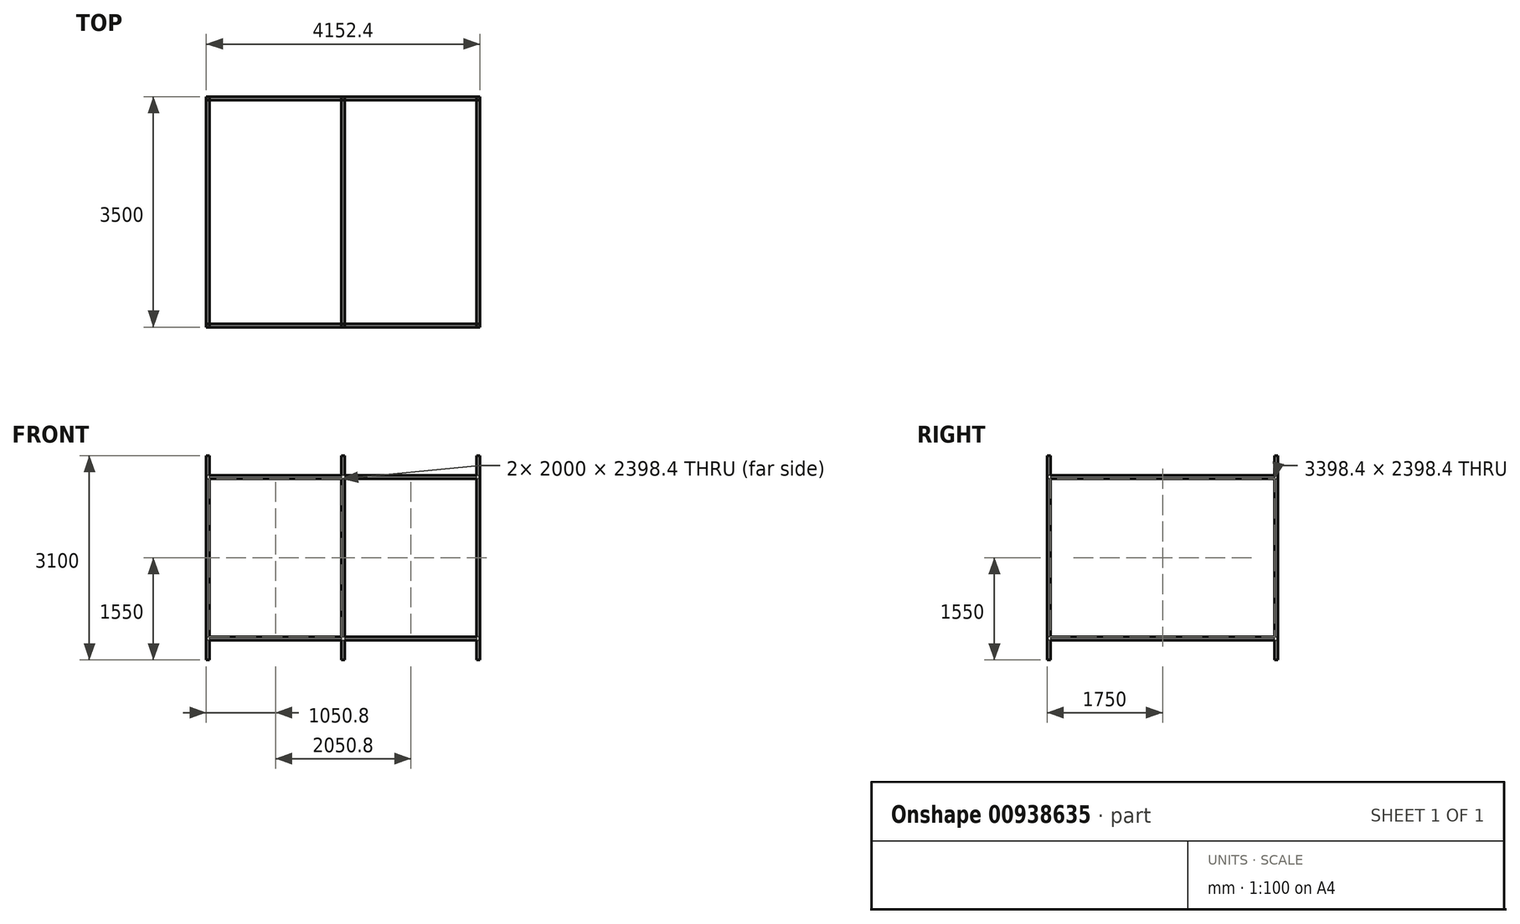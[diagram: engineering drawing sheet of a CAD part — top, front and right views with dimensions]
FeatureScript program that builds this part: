
annotation { "Feature Type Name" : "Feature", "Feature Type Description" : "" }
export const myFeature = defineFeature(function(context is Context, id is Id, definition is map)
    precondition{}
    {
        {
            var Q0;
            Q0=qCreatedBy(makeId("Right.planeOp"),FACE);
            var sketch = newSketch(context, id + "F0", { "sketchPlane" : qUnion([Q0])});
            skLineSegment(sketch, "E0.bottom", {"start": v(-1299.5, 1227.49) * mm, "end": v(2200.5, 1227.49) * mm});
            skLineSegment(sketch, "E0.top", {"start": v(-1299.5, -1272.51) * mm, "end": v(2200.5, -1272.51) * mm});
            skLineSegment(sketch, "E0.left", {"start": v(-1299.5, 1227.49) * mm, "end": v(-1299.5, -1272.51) * mm});
            skLineSegment(sketch, "E0.right", {"start": v(2200.5, 1227.49) * mm, "end": v(2200.5, -1272.51) * mm});
            skLineSegment(sketch, "E1.bottom", {"start": v(-1248.7, 1176.69) * mm, "end": v(2149.7, 1176.69) * mm});
            skLineSegment(sketch, "E1.top", {"start": v(-1248.7, -1221.71) * mm, "end": v(2149.7, -1221.71) * mm});
            skLineSegment(sketch, "E1.left", {"start": v(-1248.7, 1176.69) * mm, "end": v(-1248.7, -1221.71) * mm});
            skLineSegment(sketch, "E1.right", {"start": v(2149.7, 1176.69) * mm, "end": v(2149.7, -1221.71) * mm});
            skSolve(sketch);
        }
        {
            var Q0;
            Q0 = qSketchRegion(id + "F0", true);
            extrude(context, id + "F1", {"entities" : qUnion([Q0]), "depth" : 50.8 * mm, "offsetDistance" : 25.4 * mm});
        }
        {
            var Q0;
            Q0=makeQuery(id+"F1.opExtrude","SWEPT_FACE",FACE,{"disambiguationData":[OSD([sQuery(id+"F0.wireOp",EDGE,"E0.bottom")])]});
            var sketch = newSketch(context, id + "F2", { "sketchPlane" : qUnion([Q0])});
            skLineSegment(sketch, "E2.bottom", {"start": v(0, -1299.5) * mm, "end": v(50.8, -1299.5) * mm});
            skLineSegment(sketch, "E2.top", {"start": v(0, -1248.7) * mm, "end": v(50.8, -1248.7) * mm});
            skLineSegment(sketch, "E2.left", {"start": v(0, -1299.5) * mm, "end": v(0, -1248.7) * mm});
            skLineSegment(sketch, "E2.right", {"start": v(50.8, -1299.5) * mm, "end": v(50.8, -1248.7) * mm});
            skLineSegment(sketch, "E3.bottom", {"start": v(0, 2200.5) * mm, "end": v(50.8, 2200.5) * mm});
            skLineSegment(sketch, "E3.top", {"start": v(0, 2149.7) * mm, "end": v(50.8, 2149.7) * mm});
            skLineSegment(sketch, "E3.left", {"start": v(0, 2200.5) * mm, "end": v(0, 2149.7) * mm});
            skLineSegment(sketch, "E3.right", {"start": v(50.8, 2200.5) * mm, "end": v(50.8, 2149.7) * mm});
            skSolve(sketch);
        }
        {
            var Q0;
            Q0 = qSketchRegion(id + "F2", true);
            extrude(context, id + "F3", {"entities" : qUnion([Q0]), "operationType" : NewBodyOperationType.ADD, "depth" : 300 * mm, "offsetDistance" : 25.4 * mm});
        }
        {
            var Q0;
            Q0=makeQuery(id+"F1.opExtrude","SWEPT_FACE",FACE,{"disambiguationData":[OSD([sQuery(id+"F0.wireOp",EDGE,"E0.top")])]});
            var sketch = newSketch(context, id + "F4", { "sketchPlane" : qUnion([Q0])});
            skLineSegment(sketch, "E4.bottom", {"start": v(50.8, 1299.5) * mm, "end": v(0, 1299.5) * mm});
            skLineSegment(sketch, "E4.top", {"start": v(50.8, 1248.7) * mm, "end": v(0, 1248.7) * mm});
            skLineSegment(sketch, "E4.left", {"start": v(50.8, 1299.5) * mm, "end": v(50.8, 1248.7) * mm});
            skLineSegment(sketch, "E4.right", {"start": v(0, 1299.5) * mm, "end": v(0, 1248.7) * mm});
            skLineSegment(sketch, "E5.bottom", {"start": v(0, -2200.5) * mm, "end": v(50.8, -2200.5) * mm});
            skLineSegment(sketch, "E5.top", {"start": v(0, -2149.7) * mm, "end": v(50.8, -2149.7) * mm});
            skLineSegment(sketch, "E5.left", {"start": v(0, -2200.5) * mm, "end": v(0, -2149.7) * mm});
            skLineSegment(sketch, "E5.right", {"start": v(50.8, -2200.5) * mm, "end": v(50.8, -2149.7) * mm});
            skSolve(sketch);
        }
        {
            var Q0;
            Q0 = qSketchRegion(id + "F4", true);
            extrude(context, id + "F5", {"entities" : qUnion([Q0]), "operationType" : NewBodyOperationType.ADD, "depth" : 300 * mm, "offsetDistance" : 25.4 * mm});
        }
        {
            var Q0;
            Q0=makeQuery(id+"F5.boolean.opBoolean","MERGE",FACE,{"derivedFrom":[makeQuery(id+"F3.boolean.opBoolean","MERGE",FACE,{"derivedFrom":[makeQuery(id+"F1.opExtrude","CAP_FACE",FACE,{"disambiguationData":[OSD([sQuery(id+"F0.wireOp",EDGE,"E0.bottom"),sQuery(id+"F0.wireOp",EDGE,"E0.top"),sQuery(id+"F0.wireOp",EDGE,"E0.left"),sQuery(id+"F0.wireOp",EDGE,"E0.right"),sQuery(id+"F0.wireOp",EDGE,"E1.bottom"),sQuery(id+"F0.wireOp",EDGE,"E1.top"),sQuery(id+"F0.wireOp",EDGE,"E1.left"),sQuery(id+"F0.wireOp",EDGE,"E1.right")])],"isStart":true}),makeQuery(id+"F3.opExtrude","SWEPT_FACE",FACE,{"disambiguationData":[OSD([sQuery(id+"F2.wireOp",EDGE,"E2.left")])]}),makeQuery(id+"F3.opExtrude","SWEPT_FACE",FACE,{"disambiguationData":[OSD([sQuery(id+"F2.wireOp",EDGE,"E3.left")])]})]}),makeQuery(id+"F5.opExtrude","SWEPT_FACE",FACE,{"disambiguationData":[OSD([sQuery(id+"F4.wireOp",EDGE,"E4.right")])]}),makeQuery(id+"F5.opExtrude","SWEPT_FACE",FACE,{"disambiguationData":[OSD([sQuery(id+"F4.wireOp",EDGE,"E5.left")])]})]});
            var sketch = newSketch(context, id + "F6", { "sketchPlane" : qUnion([Q0])});
            skLineSegment(sketch, "E6.bottom", {"start": v(-2149.7, 1227.49) * mm, "end": v(-2200.5, 1227.49) * mm});
            skLineSegment(sketch, "E6.top", {"start": v(-2149.7, 1176.69) * mm, "end": v(-2200.5, 1176.69) * mm});
            skLineSegment(sketch, "E6.left", {"start": v(-2149.7, 1227.49) * mm, "end": v(-2149.7, 1176.69) * mm});
            skLineSegment(sketch, "E6.right", {"start": v(-2200.5, 1227.49) * mm, "end": v(-2200.5, 1176.69) * mm});
            skLineSegment(sketch, "E7.bottom", {"start": v(1248.7, 1176.69) * mm, "end": v(1299.5, 1176.69) * mm});
            skLineSegment(sketch, "E7.top", {"start": v(1248.7, 1227.49) * mm, "end": v(1299.5, 1227.49) * mm});
            skLineSegment(sketch, "E7.left", {"start": v(1248.7, 1176.69) * mm, "end": v(1248.7, 1227.49) * mm});
            skLineSegment(sketch, "E7.right", {"start": v(1299.5, 1176.69) * mm, "end": v(1299.5, 1227.49) * mm});
            skLineSegment(sketch, "E8.bottom", {"start": v(-2149.7, -1221.71) * mm, "end": v(-2200.5, -1221.71) * mm});
            skLineSegment(sketch, "E8.top", {"start": v(-2149.7, -1272.51) * mm, "end": v(-2200.5, -1272.51) * mm});
            skLineSegment(sketch, "E8.left", {"start": v(-2149.7, -1221.71) * mm, "end": v(-2149.7, -1272.51) * mm});
            skLineSegment(sketch, "E8.right", {"start": v(-2200.5, -1221.71) * mm, "end": v(-2200.5, -1272.51) * mm});
            skLineSegment(sketch, "E9.bottom", {"start": v(1248.7, -1221.71) * mm, "end": v(1299.5, -1221.71) * mm});
            skLineSegment(sketch, "E9.top", {"start": v(1248.7, -1272.51) * mm, "end": v(1299.5, -1272.51) * mm});
            skLineSegment(sketch, "E9.left", {"start": v(1248.7, -1221.71) * mm, "end": v(1248.7, -1272.51) * mm});
            skLineSegment(sketch, "E9.right", {"start": v(1299.5, -1221.71) * mm, "end": v(1299.5, -1272.51) * mm});
            skSolve(sketch);
        }
        {
            var Q0;
            Q0 = qSketchRegion(id + "F6", true);
            extrude(context, id + "F7", {"entities" : qUnion([Q0]), "operationType" : NewBodyOperationType.ADD, "depth" : 1000 * mm, "offsetDistance" : 25.4 * mm});
        }
        {
            var Q0;
            Q0=makeQuery(id+"F1.opExtrude","SWEPT_BODY",BODY,{"disambiguationData":[OSD([sQuery(id+"F0.wireOp",EDGE,"E0.bottom"),sQuery(id+"F0.wireOp",EDGE,"E0.top"),sQuery(id+"F0.wireOp",EDGE,"E0.left"),sQuery(id+"F0.wireOp",EDGE,"E0.right"),sQuery(id+"F0.wireOp",EDGE,"E1.bottom"),sQuery(id+"F0.wireOp",EDGE,"E1.top"),sQuery(id+"F0.wireOp",EDGE,"E1.left"),sQuery(id+"F0.wireOp",EDGE,"E1.right")])]});
            var Q1;
            Q1=makeQuery(id+"F7.opExtrude","CAP_FACE",FACE,{"disambiguationData":[OSD([sQuery(id+"F6.wireOp",EDGE,"E6.bottom"),sQuery(id+"F6.wireOp",EDGE,"E6.top"),sQuery(id+"F6.wireOp",EDGE,"E6.left"),sQuery(id+"F6.wireOp",EDGE,"E6.right")])],"isStart":false});
            mirror(context, id + "F8", {"operationType" : NewBodyOperationType.ADD, "entities" : qUnion([Q0]), "mirrorPlane" : qUnion([Q1])});
        }
        {
            var Q0;
            Q0=makeQuery(id+"F8.opPattern","COPY",FACE,{"derivedFrom":makeQuery(id+"F5.boolean.opBoolean","MERGE",FACE,{"derivedFrom":[makeQuery(id+"F3.boolean.opBoolean","MERGE",FACE,{"derivedFrom":[makeQuery(id+"F1.opExtrude","CAP_FACE",FACE,{"disambiguationData":[OSD([sQuery(id+"F0.wireOp",EDGE,"E0.bottom"),sQuery(id+"F0.wireOp",EDGE,"E0.top"),sQuery(id+"F0.wireOp",EDGE,"E0.left"),sQuery(id+"F0.wireOp",EDGE,"E0.right"),sQuery(id+"F0.wireOp",EDGE,"E1.bottom"),sQuery(id+"F0.wireOp",EDGE,"E1.top"),sQuery(id+"F0.wireOp",EDGE,"E1.left"),sQuery(id+"F0.wireOp",EDGE,"E1.right")])],"isStart":false}),makeQuery(id+"F3.opExtrude","SWEPT_FACE",FACE,{"disambiguationData":[OSD([sQuery(id+"F2.wireOp",EDGE,"E2.right")])]}),makeQuery(id+"F3.opExtrude","SWEPT_FACE",FACE,{"disambiguationData":[OSD([sQuery(id+"F2.wireOp",EDGE,"E3.right")])]})]}),makeQuery(id+"F5.opExtrude","SWEPT_FACE",FACE,{"disambiguationData":[OSD([sQuery(id+"F4.wireOp",EDGE,"E4.left")])]}),makeQuery(id+"F5.opExtrude","SWEPT_FACE",FACE,{"disambiguationData":[OSD([sQuery(id+"F4.wireOp",EDGE,"E5.right")])]})]}),"instanceName":"1"});
            var sketch = newSketch(context, id + "F9", { "sketchPlane" : qUnion([Q0])});
            skLineSegment(sketch, "E10.bottom", {"start": v(-2149.7, 1176.69) * mm, "end": v(-2200.5, 1176.69) * mm});
            skLineSegment(sketch, "E10.top", {"start": v(-2149.7, 1227.49) * mm, "end": v(-2200.5, 1227.49) * mm});
            skLineSegment(sketch, "E10.left", {"start": v(-2149.7, 1176.69) * mm, "end": v(-2149.7, 1227.49) * mm});
            skLineSegment(sketch, "E10.right", {"start": v(-2200.5, 1176.69) * mm, "end": v(-2200.5, 1227.49) * mm});
            skLineSegment(sketch, "E11.bottom", {"start": v(1248.7, 1227.49) * mm, "end": v(1299.5, 1227.49) * mm});
            skLineSegment(sketch, "E11.top", {"start": v(1248.7, 1176.69) * mm, "end": v(1299.5, 1176.69) * mm});
            skLineSegment(sketch, "E11.left", {"start": v(1248.7, 1227.49) * mm, "end": v(1248.7, 1176.69) * mm});
            skLineSegment(sketch, "E11.right", {"start": v(1299.5, 1227.49) * mm, "end": v(1299.5, 1176.69) * mm});
            skLineSegment(sketch, "E12.bottom", {"start": v(-2149.7, -1272.51) * mm, "end": v(-2200.5, -1272.51) * mm});
            skLineSegment(sketch, "E12.top", {"start": v(-2149.7, -1221.71) * mm, "end": v(-2200.5, -1221.71) * mm});
            skLineSegment(sketch, "E12.left", {"start": v(-2149.7, -1272.51) * mm, "end": v(-2149.7, -1221.71) * mm});
            skLineSegment(sketch, "E12.right", {"start": v(-2200.5, -1272.51) * mm, "end": v(-2200.5, -1221.71) * mm});
            skLineSegment(sketch, "E13.bottom", {"start": v(1248.7, -1221.71) * mm, "end": v(1299.5, -1221.71) * mm});
            skLineSegment(sketch, "E13.top", {"start": v(1248.7, -1272.51) * mm, "end": v(1299.5, -1272.51) * mm});
            skLineSegment(sketch, "E13.left", {"start": v(1248.7, -1221.71) * mm, "end": v(1248.7, -1272.51) * mm});
            skLineSegment(sketch, "E13.right", {"start": v(1299.5, -1221.71) * mm, "end": v(1299.5, -1272.51) * mm});
            skSolve(sketch);
        }
        {
            var Q0;
            Q0 = qSketchRegion(id + "F9", true);
            extrude(context, id + "F10", {"entities" : qUnion([Q0]), "operationType" : NewBodyOperationType.ADD, "depth" : 2000 * mm, "offsetDistance" : 25.4 * mm});
        }
        {
            var Q0;
            Q0=makeQuery(id+"F10.opExtrude","CAP_FACE",FACE,{"disambiguationData":[OSD([sQuery(id+"F9.wireOp",EDGE,"E10.bottom"),sQuery(id+"F9.wireOp",EDGE,"E10.top"),sQuery(id+"F9.wireOp",EDGE,"E10.left"),sQuery(id+"F9.wireOp",EDGE,"E10.right")])],"isStart":false});
            var sketch = newSketch(context, id + "F11", { "sketchPlane" : qUnion([Q0])});
            skLineSegment(sketch, "E14.bottom", {"start": v(-2200.5, 1227.49) * mm, "end": v(1299.5, 1227.49) * mm});
            skLineSegment(sketch, "E14.top", {"start": v(-2200.5, -1272.51) * mm, "end": v(1299.5, -1272.51) * mm});
            skLineSegment(sketch, "E14.left", {"start": v(-2200.5, 1227.49) * mm, "end": v(-2200.5, -1272.51) * mm});
            skLineSegment(sketch, "E14.right", {"start": v(1299.5, 1227.49) * mm, "end": v(1299.5, -1272.51) * mm});
            skLineSegment(sketch, "E15.bottom", {"start": v(-2149.7, 1176.69) * mm, "end": v(1248.7, 1176.69) * mm});
            skLineSegment(sketch, "E15.top", {"start": v(-2149.7, -1221.71) * mm, "end": v(1248.7, -1221.71) * mm});
            skLineSegment(sketch, "E15.left", {"start": v(-2149.7, 1176.69) * mm, "end": v(-2149.7, -1221.71) * mm});
            skLineSegment(sketch, "E15.right", {"start": v(1248.7, 1176.69) * mm, "end": v(1248.7, -1221.71) * mm});
            skSolve(sketch);
        }
        {
            var Q0;
            Q0 = qSketchRegion(id + "F11", true);
            extrude(context, id + "F12", {"entities" : qUnion([Q0]), "operationType" : NewBodyOperationType.ADD, "depth" : 50.8 * mm, "offsetDistance" : 25.4 * mm});
        }
        {
            var Q0;
            Q0=makeQuery(id+"F12.boolean.opBoolean","MERGE",FACE,{"derivedFrom":[makeQuery(id+"F10.opExtrude","SWEPT_FACE",FACE,{"disambiguationData":[OSD([sQuery(id+"F9.wireOp",EDGE,"E10.top")])]}),makeQuery(id+"F10.opExtrude","SWEPT_FACE",FACE,{"disambiguationData":[OSD([sQuery(id+"F9.wireOp",EDGE,"E11.bottom")])]}),makeQuery(id+"F12.opExtrude","SWEPT_FACE",FACE,{"disambiguationData":[OSD([sQuery(id+"F11.wireOp",EDGE,"E14.bottom")])]})]});
            var sketch = newSketch(context, id + "F13", { "sketchPlane" : qUnion([Q0])});
            skLineSegment(sketch, "E16.bottom", {"start": v(-4101.6, 2200.5) * mm, "end": v(-4050.8, 2200.5) * mm});
            skLineSegment(sketch, "E16.top", {"start": v(-4101.6, 2149.7) * mm, "end": v(-4050.8, 2149.7) * mm});
            skLineSegment(sketch, "E16.left", {"start": v(-4101.6, 2200.5) * mm, "end": v(-4101.6, 2149.7) * mm});
            skLineSegment(sketch, "E16.right", {"start": v(-4050.8, 2200.5) * mm, "end": v(-4050.8, 2149.7) * mm});
            skLineSegment(sketch, "E17.bottom", {"start": v(-4050.8, -1248.7) * mm, "end": v(-4101.6, -1248.7) * mm});
            skLineSegment(sketch, "E17.top", {"start": v(-4050.8, -1299.5) * mm, "end": v(-4101.6, -1299.5) * mm});
            skLineSegment(sketch, "E17.left", {"start": v(-4050.8, -1248.7) * mm, "end": v(-4050.8, -1299.5) * mm});
            skLineSegment(sketch, "E17.right", {"start": v(-4101.6, -1248.7) * mm, "end": v(-4101.6, -1299.5) * mm});
            skSolve(sketch);
        }
        {
            var Q0;
            Q0 = qSketchRegion(id + "F13", true);
            extrude(context, id + "F14", {"entities" : qUnion([Q0]), "operationType" : NewBodyOperationType.ADD, "depth" : 300 * mm, "offsetDistance" : 25.4 * mm});
        }
        {
            var Q0;
            Q0=makeQuery(id+"F12.boolean.opBoolean","MERGE",FACE,{"derivedFrom":[makeQuery(id+"F10.opExtrude","SWEPT_FACE",FACE,{"disambiguationData":[OSD([sQuery(id+"F9.wireOp",EDGE,"E12.bottom")])]}),makeQuery(id+"F10.opExtrude","SWEPT_FACE",FACE,{"disambiguationData":[OSD([sQuery(id+"F9.wireOp",EDGE,"E13.top")])]}),makeQuery(id+"F12.opExtrude","SWEPT_FACE",FACE,{"disambiguationData":[OSD([sQuery(id+"F11.wireOp",EDGE,"E14.top")])]})]});
            var sketch = newSketch(context, id + "F15", { "sketchPlane" : qUnion([Q0])});
            skLineSegment(sketch, "E18.bottom", {"start": v(-4050.8, -2149.7) * mm, "end": v(-4101.6, -2149.7) * mm});
            skLineSegment(sketch, "E18.top", {"start": v(-4050.8, -2200.5) * mm, "end": v(-4101.6, -2200.5) * mm});
            skLineSegment(sketch, "E18.left", {"start": v(-4050.8, -2149.7) * mm, "end": v(-4050.8, -2200.5) * mm});
            skLineSegment(sketch, "E18.right", {"start": v(-4101.6, -2149.7) * mm, "end": v(-4101.6, -2200.5) * mm});
            skLineSegment(sketch, "E19.bottom", {"start": v(-4050.8, 1248.7) * mm, "end": v(-4101.6, 1248.7) * mm});
            skLineSegment(sketch, "E19.top", {"start": v(-4050.8, 1299.5) * mm, "end": v(-4101.6, 1299.5) * mm});
            skLineSegment(sketch, "E19.left", {"start": v(-4050.8, 1248.7) * mm, "end": v(-4050.8, 1299.5) * mm});
            skLineSegment(sketch, "E19.right", {"start": v(-4101.6, 1248.7) * mm, "end": v(-4101.6, 1299.5) * mm});
            skSolve(sketch);
        }
        {
            var Q0;
            Q0 = qSketchRegion(id + "F15", true);
            extrude(context, id + "F16", {"entities" : qUnion([Q0]), "operationType" : NewBodyOperationType.ADD, "depth" : 300 * mm, "offsetDistance" : 25.4 * mm});
        }
    });
